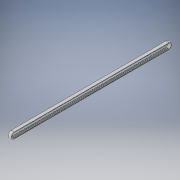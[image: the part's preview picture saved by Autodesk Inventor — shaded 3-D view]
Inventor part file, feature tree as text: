
AUTODESK INVENTOR PART (.ipt)
format: ipt  version: 2019 (Build 230136000, 136)  size: 1,482,752 bytes
history: native  units: mm
features: extrude x3, sketch x2, pattern_linear x2
ambient origin geometry x8: Origin, YZ Plane, XZ Plane, XY Plane, X Axis, Y Axis, Z Axis, Center Point
bodies: Body1 (feature_tree)
feature tree (7):
  extrude  "Extrusion2"  Depth=12.0mm
  sketch  "Sketch2"  dims[d2=306.0mm d3=8.96mm d6=6.0mm d7=0.0mm d15=1.52mm d16=0.555mm d17=0.76mm d18=0.89mm d19=0.76mm d20=0.555mm d21=1.52mm d22=2.0mm d23=0.555mm d24=0.15mm d25=6.0mm d26=0.0mm d27=1540.0mm d29=1.52mm d30=2.0mm d31=1.52mm d32=0.555mm d33=0.555mm d34=0.76mm d35=0.76mm d36=0.555mm d37=0.15mm d38=6.0mm d39=0.0mm d40=1540.0mm]
  extrude  "Extrusion3"  Depth=6.0mm
  pattern_linear  "Rectangular Pattern1"  Spacing1=6.0mm  [1 undecoded]
  extrude  "Extrusion4"  Depth=6.0mm
  pattern_linear  "Rectangular Pattern2"  Spacing1=0.555mm  [1 undecoded]
  sketch  "Sketch1"  dims[d0=306.0mm d1=12.0mm]
note: 2 required parameter values undecoded (feature->parameter linkage not recoverable at this tier; creation-order binding heuristic only, values carry confidence <= 0.55)
